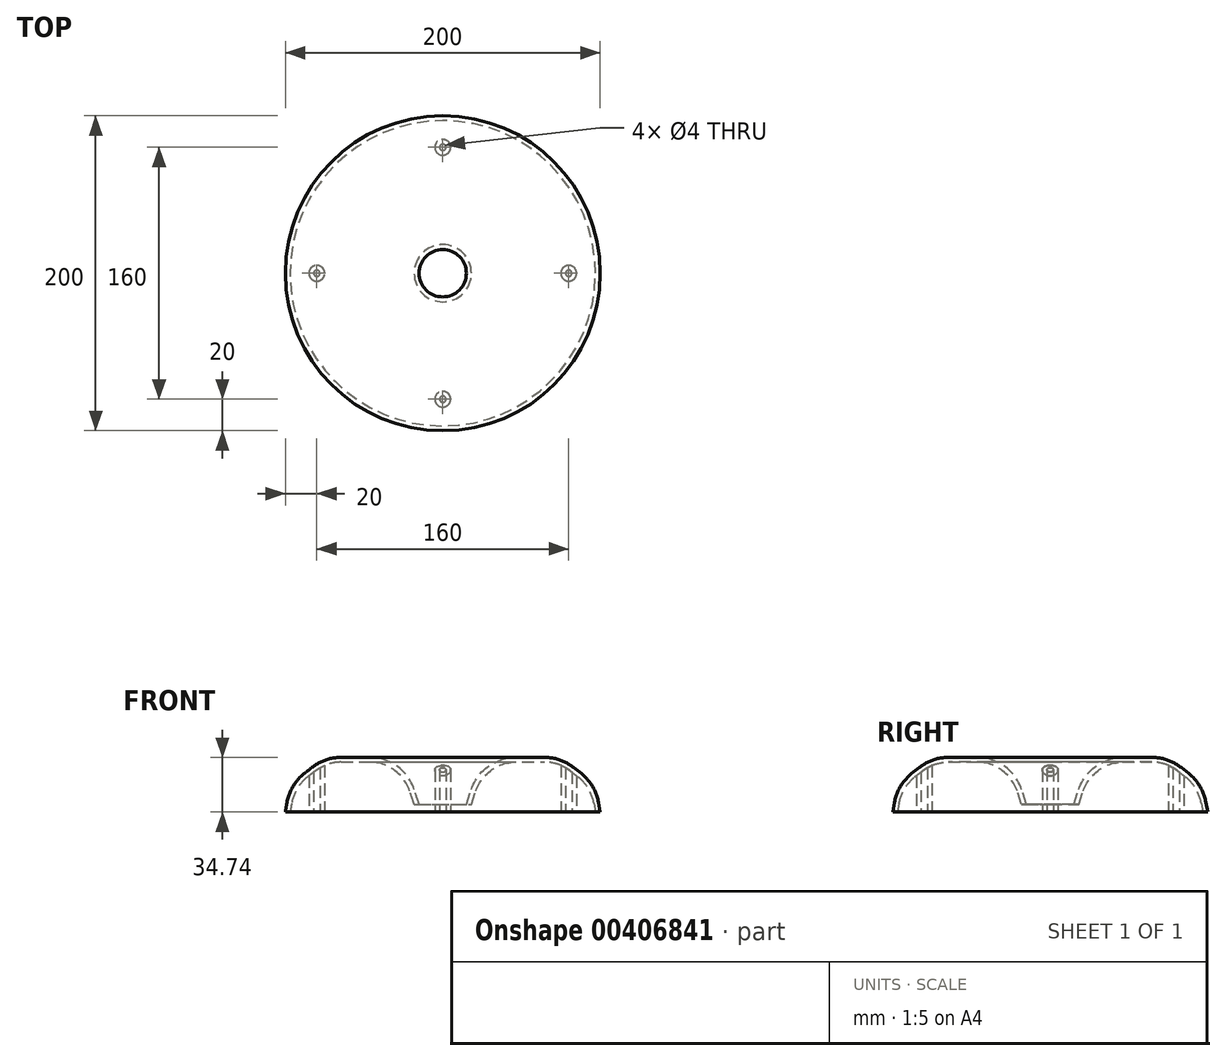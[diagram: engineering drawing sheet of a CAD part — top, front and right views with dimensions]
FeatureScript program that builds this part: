
annotation { "Feature Type Name" : "Feature", "Feature Type Description" : "" }
export const myFeature = defineFeature(function(context is Context, id is Id, definition is map)
    precondition{}
    {
        {
            var Q0;
            Q0=qCreatedBy(makeId("Front.planeOp"),FACE);
            var sketch = newSketch(context, id + "F0", { "sketchPlane" : qUnion([Q0])});
            skLineSegment(sketch, "E0", {"start": v(0, 0) * mm, "end": v(-100, 0) * mm, "construction": true});
            skLineSegment(sketch, "E1", {"start": v(-64.55, 34.74) * mm, "end": v(-46.56, 34.74) * mm});
            skLineSegment(sketch, "E2", {"start": v(-18.13, 14.3) * mm, "end": v(-15, 5) * mm});
            skPoint(sketch, "E3.visualSharp", {"position": v(-25, 34.74) * mm});
            skArc(sketch, "E3.filletArc", {"start": v(-18.13, 14.3) * mm, "mid": v(-29.05, 29.1) * mm, "end": v(-46.56, 34.74) * mm});
            skLineSegment(sketch, "E4", {"start": v(-83.19, 28.25) * mm, "end": v(-88, 24.44) * mm});
            skPoint(sketch, "E5.visualSharp", {"position": v(-75, 34.74) * mm});
            skArc(sketch, "E5.filletArc", {"start": v(-64.55, 34.74) * mm, "mid": v(-74.42, 33.07) * mm, "end": v(-83.19, 28.25) * mm});
            skLineSegment(sketch, "E6", {"start": v(-98.9, 6.2) * mm, "end": v(-100, 0) * mm});
            skPoint(sketch, "E7.visualSharp", {"position": v(-96.9, 17.38) * mm});
            skArc(sketch, "E7.filletArc", {"start": v(-88, 24.44) * mm, "mid": v(-95.12, 16.31) * mm, "end": v(-98.9, 6.2) * mm});
            skLineSegment(sketch, "E8.0", {"start": v(-95.94, 5.66) * mm, "end": v(-96.95, 0) * mm});
            skArc(sketch, "E8.1", {"start": v(-86.13, 22.09) * mm, "mid": v(-92.54, 14.77) * mm, "end": v(-95.94, 5.66) * mm});
            skLineSegment(sketch, "E8.2", {"start": v(-81.32, 25.9) * mm, "end": v(-86.13, 22.09) * mm});
            skLineSegment(sketch, "E8.3", {"start": v(-20.97, 13.34) * mm, "end": v(-18.17, 5) * mm});
            skArc(sketch, "E8.4", {"start": v(-20.97, 13.34) * mm, "mid": v(-30.8, 26.66) * mm, "end": v(-46.56, 31.74) * mm});
            skLineSegment(sketch, "E8.5", {"start": v(-64.55, 31.74) * mm, "end": v(-46.56, 31.74) * mm});
            skArc(sketch, "E8.6", {"start": v(-64.55, 31.74) * mm, "mid": v(-73.43, 30.24) * mm, "end": v(-81.32, 25.9) * mm});
            skLineSegment(sketch, "E9", {"start": v(-100, 0) * mm, "end": v(-96.95, 0) * mm});
            skLineSegment(sketch, "E10", {"start": v(-18.17, 5) * mm, "end": v(-15, 5) * mm});
            skLineSegment(sketch, "E11", {"start": v(0, 0) * mm, "end": v(0, 53.57) * mm, "construction": true});
            skSolve(sketch);
        }
        {
            var Q0;
            Q0 = qSketchRegion(id + "F0", true);
            var Q1;
            Q1=sQuery(id+"F0.wireOp",EDGE,"E11");
            revolve(context, id + "F1", {"entities" : qUnion([Q0]), "axis" : qUnion([Q1]), "revolveType" : RevolveType.FULL});
        }
        {
            var Q0;
            Q0=makeQuery(id+"F1.opRevolve","SWEPT_FACE",FACE,{"disambiguationData":[OSD([sQuery(id+"F0.wireOp",EDGE,"E9")])]});
            var sketch = newSketch(context, id + "F2", { "sketchPlane" : qUnion([Q0])});
            skCircle(sketch, "E12", {"center": v(80, 0) * mm, "radius": 5 * mm});
            skCircle(sketch, "E13", {"center": v(80, 0) * mm, "radius": 2 * mm});
            skCircle(sketch, "E14.1.0", {"center": v(0, 80) * mm, "radius": 5 * mm});
            skCircle(sketch, "E14.1.1", {"center": v(0, 80) * mm, "radius": 2 * mm});
            skCircle(sketch, "E14.2.0", {"center": v(-80, 0) * mm, "radius": 5 * mm});
            skCircle(sketch, "E14.2.1", {"center": v(-80, 0) * mm, "radius": 2 * mm});
            skCircle(sketch, "E14.3.0", {"center": v(0, -80) * mm, "radius": 5 * mm});
            skCircle(sketch, "E14.3.1", {"center": v(0, -80) * mm, "radius": 2 * mm});
            skPoint(sketch, "E14.center", {"position": v(0, 0) * mm});
            skSolve(sketch);
        }
        {
            var Q0;
            Q0 = qSketchRegion(id + "F2", true);
            extrude(context, id + "F3", {"entities" : qUnion([Q0]), "operationType" : NewBodyOperationType.ADD, "endBound" : BoundingType.UP_TO_NEXT, "oppositeDirection" : true, "depth" : 25 * mm});
        }
    });
